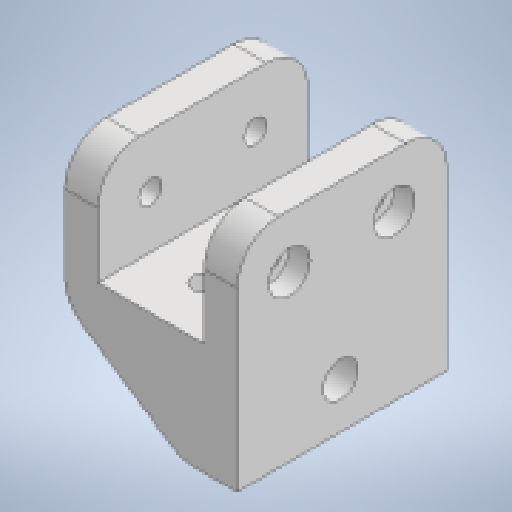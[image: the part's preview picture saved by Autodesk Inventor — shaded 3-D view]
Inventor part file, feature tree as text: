
AUTODESK INVENTOR PART (.ipt)
format: ipt  version: 2025 (Build 290162000, 162)  size: 253,952 bytes
history: native  units: mm
features: projected_geometry x9, extrude x8, sketch x8, other x3, fillet x2, reference x1
ambient origin geometry x8: Origin, YZ Plane, XZ Plane, XY Plane, X Axis, Y Axis, Z Axis, Center Point
bodies: Solid1 (feature_tree)
feature tree (31):
  extrude  "Extrusion1"  Depth=25.654mm
  extrude  "Extrusion2"  Depth=50.8mm TaperAngle=0.0deg
  extrude  "Extrusion3"  Depth=8.5mm
  extrude  "Extrusion4"  TaperAngle=0.0deg  [1 undecoded]
  extrude  "Extrusion5"  TaperAngle=0.0deg  [1 undecoded]
  extrude  "Extrusion6"  TaperAngle=0.0deg  [1 undecoded]
  extrude  "Extrusion7"  Depth=10.0mm
  fillet  "Fillet1"  Radius=5.0mm
  extrude  "Extrusion8"  Depth=6.0mm TaperAngle=0.0deg
  fillet  "Fillet2"  Radius=6.0mm
  sketch  "Sketch1"  dims[d0=25.654mm d1=25.654mm]
  sketch  "Sketch2"  dims[d2=8.0mm d3=50.8mm d4=0.0mm]
  projected_geometry  "Projected Loop1"
  sketch  "Sketch3"  dims[d5=19.05mm d6=0.0mm d7=8.5mm]
  projected_geometry  "Projected Loop2"
  sketch  "Sketch4"  dims[d8=25.4mm d9=0.0mm d10=0.0mm d11=0.0mm]
  projected_geometry  "Projected Loop3"
  sketch  "Sketch5"  dims[d12=5.5mm d13=0.0mm d14=0.0mm]
  reference  "Reference1"
  projected_geometry  "Projected Loop4"
  sketch  "Sketch6"  dims[d15=5.5mm d16=0.0mm d17=0.0mm]
  projected_geometry  "Projected Loop5"
  projected_geometry  "Projected Loop6"
  projected_geometry  "Projected Loop7"
  sketch  "Sketch7"  dims[d18=10.0mm d19=10.0mm d20=5.0mm d21=0.0mm]
  projected_geometry  "Projected Loop8"
  sketch  "Sketch8"  dims[d22=10.0mm d23=4.0mm d24=0.0mm d25=6.0mm]
  projected_geometry  "Projected Loop9"
  other  "<userpath>\Desktop\puppycat\singleSwingarmV2.iam"
  other  "singleSwingarmV2.iam"
  other  "trackBase:1"
note: 3 required parameter values undecoded (feature->parameter linkage not recoverable at this tier; creation-order binding heuristic only, values carry confidence <= 0.55)
